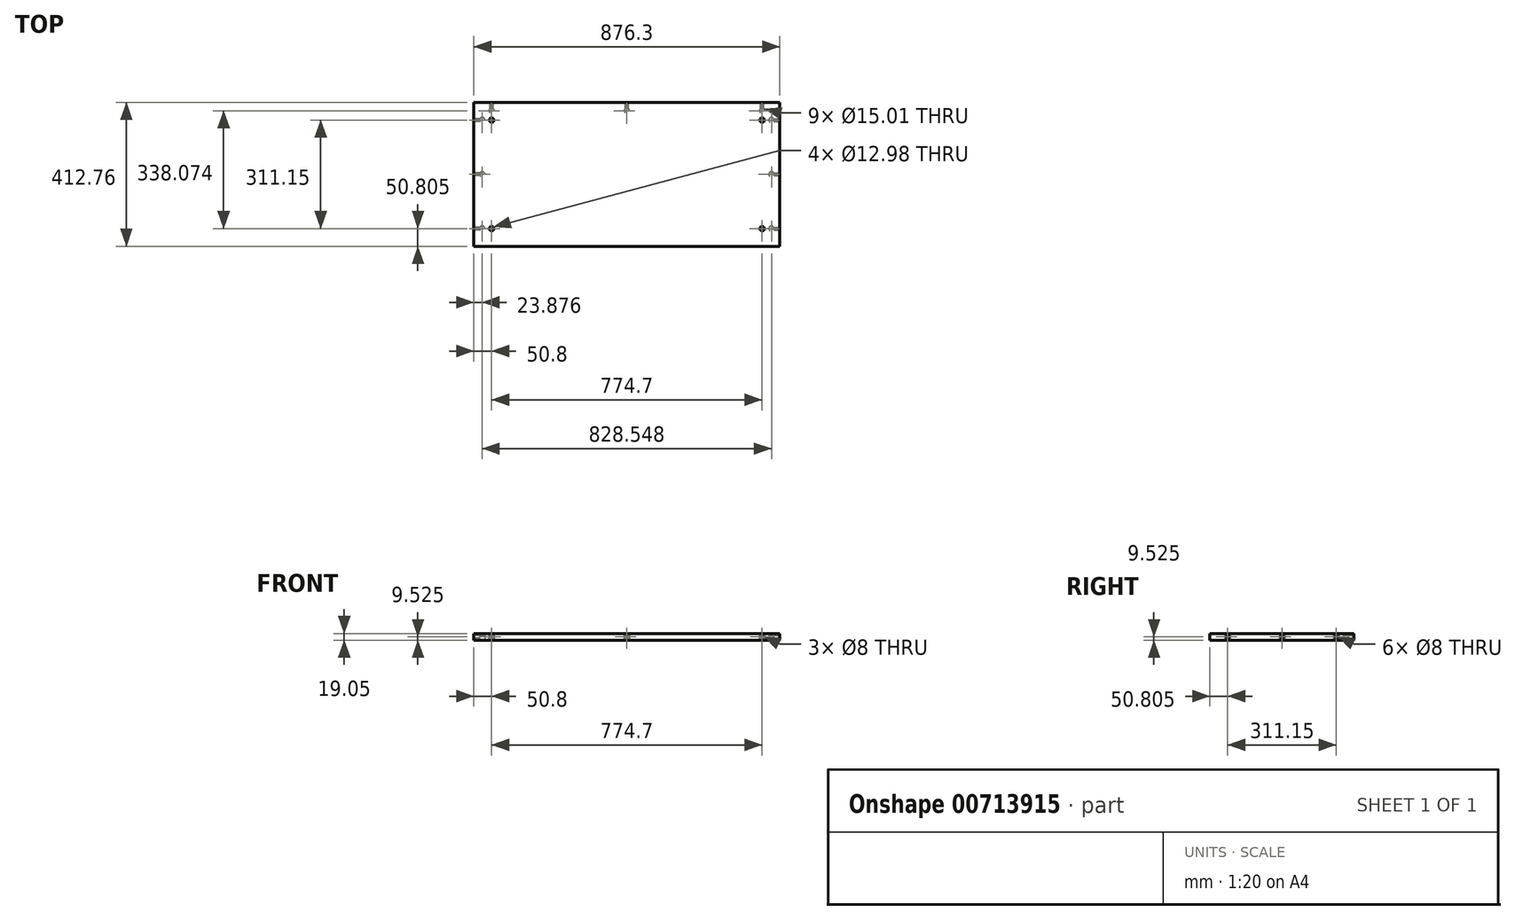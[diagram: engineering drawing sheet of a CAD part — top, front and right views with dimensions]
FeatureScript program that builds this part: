
annotation { "Feature Type Name" : "Feature", "Feature Type Description" : "" }
export const myFeature = defineFeature(function(context is Context, id is Id, definition is map)
    precondition{}
    {
        {
            var Q0;
            Q0=qCreatedBy(makeId("Top.planeOp"),FACE);
            var sketch = newSketch(context, id + "F0", { "sketchPlane" : qUnion([Q0])});
            skLineSegment(sketch, "E0.bottom", {"start": v(438.15, 206.38) * mm, "end": v(-438.15, 206.38) * mm});
            skLineSegment(sketch, "E0.top", {"start": v(438.15, -206.38) * mm, "end": v(-438.15, -206.38) * mm});
            skLineSegment(sketch, "E0.left", {"start": v(438.15, 206.37) * mm, "end": v(438.15, -206.38) * mm});
            skLineSegment(sketch, "E0.right", {"start": v(-438.15, 206.38) * mm, "end": v(-438.15, -206.38) * mm});
            skPoint(sketch, "E0.middle", {"position": v(0, 0) * mm});
            skSolve(sketch);
        }
        {
            var Q0;
            Q0=makeQuery(id+"F0.imprint","IMPRINT",FACE,{"disambiguationData":[TD([[makeQuery(id+"F0.imprint","IMPRINT",EDGE,{"derivedFrom":sQuery(id+"F0.wireOp",EDGE,"E0.bottom")}),1.0]])]});
            extrude(context, id + "F1", {"entities" : qUnion([Q0]), "depth" : 19.05 * mm, "offsetDistance" : 25.4 * mm});
        }
        {
            var Q0;
            Q0=makeQuery(id+"F1.opExtrude","CAP_FACE",FACE,{"disambiguationData":[OSD([sQuery(id+"F0.wireOp",EDGE,"E0.bottom"),sQuery(id+"F0.wireOp",EDGE,"E0.top"),sQuery(id+"F0.wireOp",EDGE,"E0.left"),sQuery(id+"F0.wireOp",EDGE,"E0.right")])],"isStart":true});
            var sketch = newSketch(context, id + "F2", { "sketchPlane" : qUnion([Q0])});
            skLineSegment(sketch, "E1", {"start": v(-438.15, 206.38) * mm, "end": v(-414.27, 206.38) * mm});
            skLineSegment(sketch, "E2", {"start": v(-414.27, 206.38) * mm, "end": v(-414.27, -206.38) * mm});
            skLineSegment(sketch, "E3", {"start": v(438.15, 206.38) * mm, "end": v(414.27, 206.38) * mm});
            skLineSegment(sketch, "E4", {"start": v(414.27, 206.38) * mm, "end": v(414.27, -206.38) * mm});
            skLineSegment(sketch, "E5", {"start": v(-438.15, -206.38) * mm, "end": v(-438.15, -182.5) * mm});
            skLineSegment(sketch, "E6", {"start": v(-438.15, -182.5) * mm, "end": v(438.15, -182.5) * mm});
            skLineSegment(sketch, "E7", {"start": v(-438.15, -182.5) * mm, "end": v(-387.35, -182.5) * mm});
            skLineSegment(sketch, "E8", {"start": v(438.15, -182.5) * mm, "end": v(387.35, -182.5) * mm});
            skLineSegment(sketch, "E9", {"start": v(0, -206.38) * mm, "end": v(0, -182.5) * mm});
            skLineSegment(sketch, "E10", {"start": v(-414.27, 206.38) * mm, "end": v(-414.27, 155.58) * mm});
            skLineSegment(sketch, "E11", {"start": v(414.27, 206.38) * mm, "end": v(414.27, 155.58) * mm});
            skLineSegment(sketch, "E12", {"start": v(-414.27, -206.38) * mm, "end": v(-414.27, -155.57) * mm});
            skLineSegment(sketch, "E13", {"start": v(414.27, -206.38) * mm, "end": v(414.27, -155.57) * mm});
            skLineSegment(sketch, "E14", {"start": v(-438.15, 0) * mm, "end": v(-414.27, 0) * mm});
            skLineSegment(sketch, "E15", {"start": v(438.15, 0) * mm, "end": v(414.27, 0) * mm});
            skPoint(sketch, "E16", {"position": v(-414.27, 155.58) * mm});
            skPoint(sketch, "E17", {"position": v(-414.27, 0) * mm});
            skPoint(sketch, "E18", {"position": v(-414.27, -155.57) * mm});
            skPoint(sketch, "E19", {"position": v(-387.35, -182.5) * mm});
            skPoint(sketch, "E20", {"position": v(0, -182.5) * mm});
            skPoint(sketch, "E21", {"position": v(414.27, -155.57) * mm});
            skPoint(sketch, "E22", {"position": v(387.35, -182.5) * mm});
            skPoint(sketch, "E23", {"position": v(414.27, 0) * mm});
            skPoint(sketch, "E24", {"position": v(414.27, 155.58) * mm});
            skSolve(sketch);
        }
        {
            var Q0;
            Q0=sQuery(id+"F2.wireOp",VERTEX,"E16");
            var Q1;
            Q1=sQuery(id+"F2.wireOp",VERTEX,"E17");
            var Q2;
            Q2=sQuery(id+"F2.wireOp",VERTEX,"E18");
            var Q3;
            Q3=sQuery(id+"F2.wireOp",VERTEX,"E19");
            var Q4;
            Q4=sQuery(id+"F2.wireOp",VERTEX,"E20");
            var Q5;
            Q5=sQuery(id+"F2.wireOp",VERTEX,"E22");
            var Q6;
            Q6=sQuery(id+"F2.wireOp",VERTEX,"E21");
            var Q7;
            Q7=sQuery(id+"F2.wireOp",VERTEX,"E23");
            var Q8;
            Q8=sQuery(id+"F2.wireOp",VERTEX,"E24");
            var Q9;
            Q9=makeQuery(id+"F1.opExtrude","SWEPT_BODY",BODY,{"disambiguationData":[OSD([sQuery(id+"F0.wireOp",EDGE,"E0.bottom"),sQuery(id+"F0.wireOp",EDGE,"E0.top"),sQuery(id+"F0.wireOp",EDGE,"E0.left"),sQuery(id+"F0.wireOp",EDGE,"E0.right")])]});
            hole(context, id + "F3", {"style" : HoleStyle.SIMPLE, "endStyle" : HoleEndStyle.BLIND, "holeDiameter" : 15 * mm, "majorDiameter" : 6.35 * mm, "holeDepth" : 14.22 * mm, "isTappedThrough" : true, "tappedDepth" : 12.7 * mm, "tapClearance" : 3, "startFromSketch" : true, "locations" : qUnion([Q0, Q1, Q2, Q3, Q4, Q5, Q6, Q7, Q8]), "scope" : qUnion([Q9])});
        }
        {
            var Q0;
            Q0=makeQuery(id+"F1.opExtrude","SWEPT_FACE",FACE,{"disambiguationData":[OSD([sQuery(id+"F0.wireOp",EDGE,"E0.bottom")])]});
            var sketch = newSketch(context, id + "F4", { "sketchPlane" : qUnion([Q0])});
            skLineSegment(sketch, "E25", {"start": v(-438.15, 9.53) * mm, "end": v(-387.35, 9.53) * mm});
            skLineSegment(sketch, "E26", {"start": v(438.15, 9.53) * mm, "end": v(387.35, 9.53) * mm});
            skLineSegment(sketch, "E27", {"start": v(0, 0) * mm, "end": v(0, 9.53) * mm});
            skPoint(sketch, "E28", {"position": v(-387.35, 9.53) * mm});
            skPoint(sketch, "E29", {"position": v(0, 9.53) * mm});
            skPoint(sketch, "E30", {"position": v(387.35, 9.53) * mm});
            skSolve(sketch);
        }
        {
            var Q0;
            Q0=sQuery(id+"F4.wireOp",VERTEX,"E28");
            var Q1;
            Q1=sQuery(id+"F4.wireOp",VERTEX,"E29");
            var Q2;
            Q2=sQuery(id+"F4.wireOp",VERTEX,"E30");
            var Q3;
            Q3=makeQuery(id+"F1.opExtrude","SWEPT_BODY",BODY,{"disambiguationData":[OSD([sQuery(id+"F0.wireOp",EDGE,"E0.bottom"),sQuery(id+"F0.wireOp",EDGE,"E0.top"),sQuery(id+"F0.wireOp",EDGE,"E0.left"),sQuery(id+"F0.wireOp",EDGE,"E0.right")])]});
            hole(context, id + "F5", {"style" : HoleStyle.SIMPLE, "endStyle" : HoleEndStyle.BLIND, "holeDiameter" : 8 * mm, "majorDiameter" : 6.35 * mm, "holeDepth" : 25.4 * mm, "isTappedThrough" : true, "tappedDepth" : 12.7 * mm, "tapClearance" : 3, "startFromSketch" : true, "locations" : qUnion([Q0, Q1, Q2]), "scope" : qUnion([Q3])});
        }
        {
            var Q0;
            Q0=makeQuery(id+"F1.opExtrude","SWEPT_FACE",FACE,{"disambiguationData":[OSD([sQuery(id+"F0.wireOp",EDGE,"E0.right")])]});
            var sketch = newSketch(context, id + "F6", { "sketchPlane" : qUnion([Q0])});
            skLineSegment(sketch, "E31", {"start": v(-206.37, 9.53) * mm, "end": v(-155.57, 9.53) * mm});
            skLineSegment(sketch, "E32", {"start": v(206.38, 9.53) * mm, "end": v(155.58, 9.53) * mm});
            skLineSegment(sketch, "E33", {"start": v(0, 0) * mm, "end": v(0, 9.53) * mm});
            skPoint(sketch, "E34", {"position": v(-155.57, 9.53) * mm});
            skPoint(sketch, "E35", {"position": v(0, 9.53) * mm});
            skPoint(sketch, "E36", {"position": v(155.58, 9.53) * mm});
            skSolve(sketch);
        }
        {
            var Q0;
            Q0=sQuery(id+"F6.wireOp",VERTEX,"E34");
            var Q1;
            Q1=sQuery(id+"F6.wireOp",VERTEX,"E35");
            var Q2;
            Q2=sQuery(id+"F6.wireOp",VERTEX,"E36");
            var Q3;
            Q3=makeQuery(id+"F1.opExtrude","SWEPT_BODY",BODY,{"disambiguationData":[OSD([sQuery(id+"F0.wireOp",EDGE,"E0.bottom"),sQuery(id+"F0.wireOp",EDGE,"E0.top"),sQuery(id+"F0.wireOp",EDGE,"E0.left"),sQuery(id+"F0.wireOp",EDGE,"E0.right")])]});
            hole(context, id + "F7", {"style" : HoleStyle.SIMPLE, "endStyle" : HoleEndStyle.BLIND, "holeDiameter" : 8 * mm, "majorDiameter" : 6.35 * mm, "holeDepth" : 25.4 * mm, "isTappedThrough" : true, "tappedDepth" : 12.7 * mm, "tapClearance" : 3, "startFromSketch" : true, "locations" : qUnion([Q0, Q1, Q2]), "scope" : qUnion([Q3])});
        }
        {
            var Q0;
            Q0=makeQuery(id+"F1.opExtrude","SWEPT_FACE",FACE,{"disambiguationData":[OSD([sQuery(id+"F0.wireOp",EDGE,"E0.left")])]});
            var sketch = newSketch(context, id + "F8", { "sketchPlane" : qUnion([Q0])});
            skLineSegment(sketch, "E37", {"start": v(-206.38, 9.53) * mm, "end": v(-155.58, 9.53) * mm});
            skLineSegment(sketch, "E38", {"start": v(206.38, 9.53) * mm, "end": v(155.58, 9.53) * mm});
            skLineSegment(sketch, "E39", {"start": v(0, 0) * mm, "end": v(0, 9.53) * mm});
            skPoint(sketch, "E40", {"position": v(-155.58, 9.53) * mm});
            skPoint(sketch, "E41", {"position": v(0, 9.53) * mm});
            skPoint(sketch, "E42", {"position": v(155.58, 9.53) * mm});
            skSolve(sketch);
        }
        {
            var Q0;
            Q0=sQuery(id+"F8.wireOp",VERTEX,"E40");
            var Q1;
            Q1=sQuery(id+"F8.wireOp",VERTEX,"E41");
            var Q2;
            Q2=sQuery(id+"F8.wireOp",VERTEX,"E42");
            var Q3;
            Q3=makeQuery(id+"F1.opExtrude","SWEPT_BODY",BODY,{"disambiguationData":[OSD([sQuery(id+"F0.wireOp",EDGE,"E0.bottom"),sQuery(id+"F0.wireOp",EDGE,"E0.top"),sQuery(id+"F0.wireOp",EDGE,"E0.left"),sQuery(id+"F0.wireOp",EDGE,"E0.right")])]});
            hole(context, id + "F9", {"style" : HoleStyle.SIMPLE, "endStyle" : HoleEndStyle.BLIND, "holeDiameter" : 8 * mm, "majorDiameter" : 6.35 * mm, "holeDepth" : 25.4 * mm, "isTappedThrough" : true, "tappedDepth" : 12.7 * mm, "tapClearance" : 3, "startFromSketch" : true, "locations" : qUnion([Q0, Q1, Q2]), "scope" : qUnion([Q3])});
        }
        {
            var Q0;
            Q0=makeQuery(id+"F1.opExtrude","CAP_FACE",FACE,{"disambiguationData":[OSD([sQuery(id+"F0.wireOp",EDGE,"E0.bottom"),sQuery(id+"F0.wireOp",EDGE,"E0.top"),sQuery(id+"F0.wireOp",EDGE,"E0.left"),sQuery(id+"F0.wireOp",EDGE,"E0.right")])],"isStart":false});
            var sketch = newSketch(context, id + "F10", { "sketchPlane" : qUnion([Q0])});
            skLineSegment(sketch, "E43.bottom", {"start": v(387.35, 155.58) * mm, "end": v(-387.35, 155.58) * mm});
            skLineSegment(sketch, "E43.top", {"start": v(387.35, -155.58) * mm, "end": v(-387.35, -155.58) * mm});
            skLineSegment(sketch, "E43.left", {"start": v(387.35, 155.58) * mm, "end": v(387.35, -155.58) * mm});
            skLineSegment(sketch, "E43.right", {"start": v(-387.35, 155.58) * mm, "end": v(-387.35, -155.58) * mm});
            skPoint(sketch, "E43.middle", {"position": v(0, 0) * mm});
            skPoint(sketch, "E44", {"position": v(-387.35, 155.58) * mm});
            skPoint(sketch, "E45", {"position": v(387.35, 155.58) * mm});
            skPoint(sketch, "E46", {"position": v(387.35, -155.58) * mm});
            skPoint(sketch, "E47", {"position": v(-387.35, -155.58) * mm});
            skSolve(sketch);
        }
        {
            var Q0;
            Q0=sQuery(id+"F10.wireOp",VERTEX,"E44");
            var Q1;
            Q1=sQuery(id+"F10.wireOp",VERTEX,"E45");
            var Q2;
            Q2=sQuery(id+"F10.wireOp",VERTEX,"E46");
            var Q3;
            Q3=sQuery(id+"F10.wireOp",VERTEX,"E47");
            var Q4;
            Q4=makeQuery(id+"F1.opExtrude","SWEPT_BODY",BODY,{"disambiguationData":[OSD([sQuery(id+"F0.wireOp",EDGE,"E0.bottom"),sQuery(id+"F0.wireOp",EDGE,"E0.top"),sQuery(id+"F0.wireOp",EDGE,"E0.left"),sQuery(id+"F0.wireOp",EDGE,"E0.right")])]});
            hole(context, id + "F11", {"style" : HoleStyle.SIMPLE, "endStyle" : HoleEndStyle.BLIND, "holeDiameter" : 12.98 * mm, "majorDiameter" : 6.35 * mm, "holeDepth" : 25.4 * mm, "isTappedThrough" : true, "tappedDepth" : 12.7 * mm, "tapClearance" : 3, "startFromSketch" : true, "locations" : qUnion([Q0, Q1, Q2, Q3]), "scope" : qUnion([Q4])});
        }
    });
